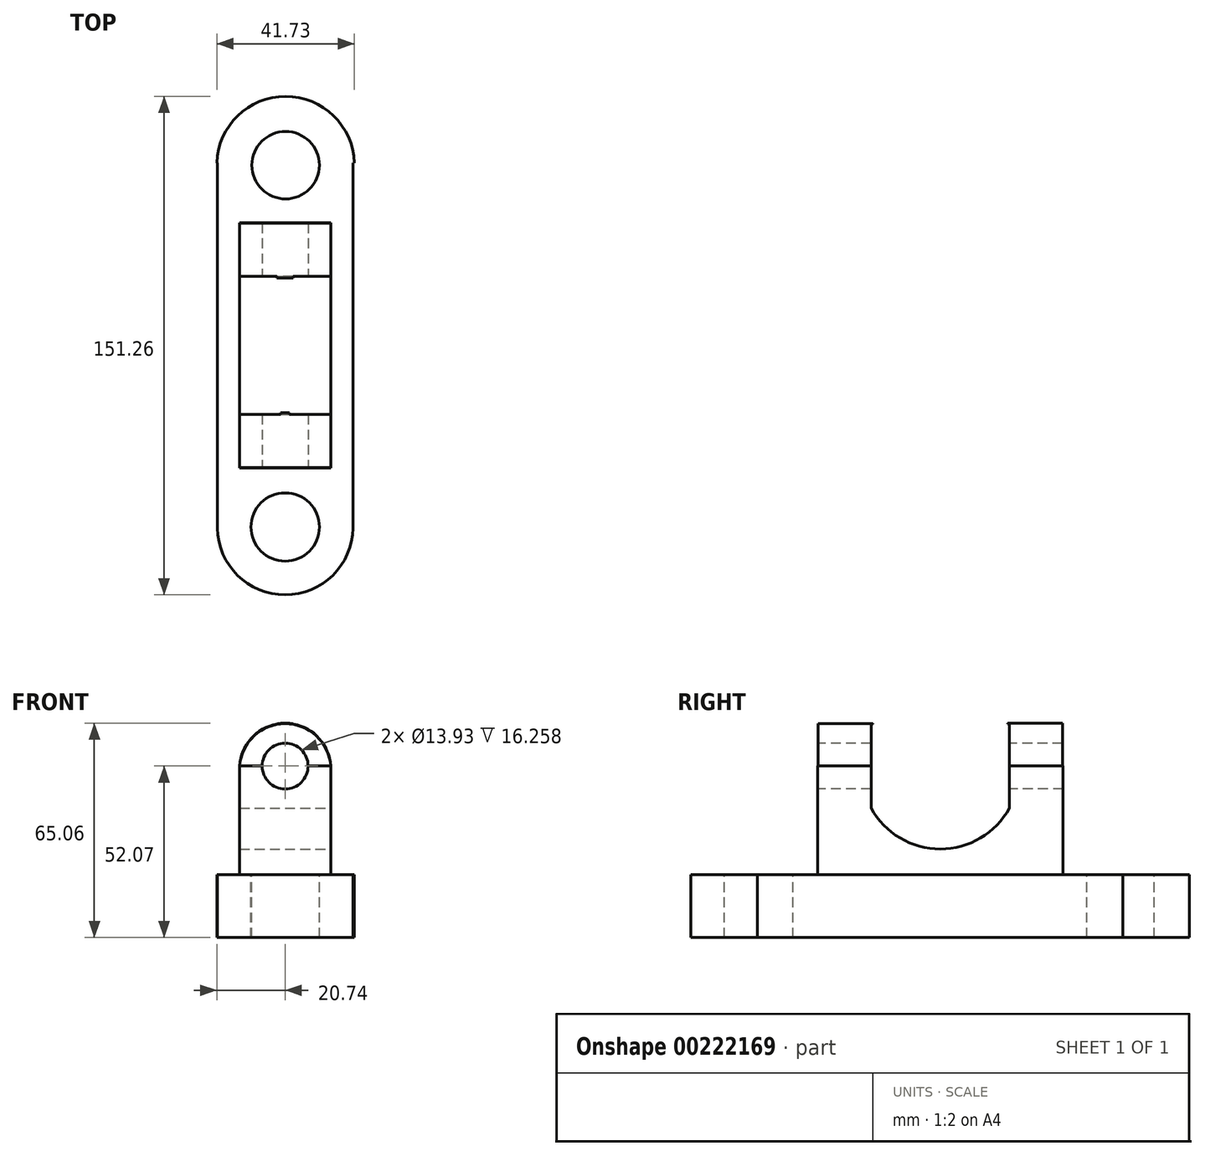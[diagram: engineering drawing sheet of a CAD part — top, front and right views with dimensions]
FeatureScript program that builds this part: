
annotation { "Feature Type Name" : "Feature", "Feature Type Description" : "" }
export const myFeature = defineFeature(function(context is Context, id is Id, definition is map)
    precondition{}
    {
        {
            var Q0;
            Q0=qCreatedBy(makeId("Top.planeOp"),FACE);
            var sketch = newSketch(context, id + "F0", { "sketchPlane" : qUnion([Q0])});
            skLineSegment(sketch, "E0.bottom", {"start": v(20.56, -55.45) * mm, "end": v(-20.56, -55.45) * mm});
            skLineSegment(sketch, "E0.top", {"start": v(20.56, 55.45) * mm, "end": v(-20.56, 55.45) * mm});
            skLineSegment(sketch, "E0.left", {"start": v(20.56, -55.45) * mm, "end": v(20.56, 55.45) * mm});
            skLineSegment(sketch, "E0.right", {"start": v(-20.56, -55.45) * mm, "end": v(-20.56, 55.45) * mm});
            skPoint(sketch, "E0.middle", {"position": v(0, 0) * mm});
            skSolve(sketch);
        }
        {
            var Q0;
            Q0 = qSketchRegion(id + "F0", true);
            extrude(context, id + "F1", {"entities" : qUnion([Q0]), "depth" : 19.05 * mm});
        }
        {
            var Q0;
            Q0=qCreatedBy(makeId("Top.planeOp"),FACE);
            var sketch = newSketch(context, id + "F2", { "sketchPlane" : qUnion([Q0])});
            skArc(sketch, "E1", {"start": v(21, 55.43) * mm, "mid": v(0.13, 75.58) * mm, "end": v(-20.74, 55.43) * mm});
            skLineSegment(sketch, "E2", {"start": v(-20.74, 55.43) * mm, "end": v(21, 55.43) * mm});
            skSolve(sketch);
        }
        {
            var Q0;
            Q0=makeQuery(id+"F2.imprint","IMPRINT",FACE,{"disambiguationData":[TD([[makeQuery(id+"F2.imprint","IMPRINT",EDGE,{"derivedFrom":sQuery(id+"F2.wireOp",EDGE,"E1")}),1.0]])]});
            extrude(context, id + "F3", {"entities" : qUnion([Q0]), "operationType" : NewBodyOperationType.ADD, "depth" : 19.05 * mm});
        }
        {
            var Q0;
            Q0=qCreatedBy(makeId("Top.planeOp"),FACE);
            var sketch = newSketch(context, id + "F4", { "sketchPlane" : qUnion([Q0])});
            skLineSegment(sketch, "E3.0", {"start": v(20.56, -55.45) * mm, "end": v(-20.56, -55.45) * mm});
            skArc(sketch, "E4", {"start": v(-20.56, -55.45) * mm, "mid": v(0, -75.68) * mm, "end": v(20.56, -55.45) * mm});
            skSolve(sketch);
        }
        {
            var Q0;
            Q0 = qSketchRegion(id + "F4", true);
            extrude(context, id + "F5", {"entities" : qUnion([Q0]), "operationType" : NewBodyOperationType.ADD, "depth" : 19.05 * mm});
        }
        {
            var Q0;
            Q0=makeQuery(id+"F5.boolean.opBoolean","MERGE",FACE,{"derivedFrom":[makeQuery(id+"F3.boolean.opBoolean","MERGE",FACE,{"derivedFrom":[makeQuery(id+"F1.opExtrude","CAP_FACE",FACE,{"disambiguationData":[OSD([sQuery(id+"F0.wireOp",EDGE,"E0.bottom"),sQuery(id+"F0.wireOp",EDGE,"E0.top"),sQuery(id+"F0.wireOp",EDGE,"E0.left"),sQuery(id+"F0.wireOp",EDGE,"E0.right")])],"isStart":false}),makeQuery(id+"F3.opExtrude","CAP_FACE",FACE,{"disambiguationData":[OSD([sQuery(id+"F2.wireOp",EDGE,"E1"),sQuery(id+"F2.wireOp",EDGE,"E2")])],"isStart":false})]}),makeQuery(id+"F5.opExtrude","CAP_FACE",FACE,{"disambiguationData":[OSD([sQuery(id+"F4.wireOp",EDGE,"E3.0"),sQuery(id+"F4.wireOp",EDGE,"E4")])],"isStart":false})]});
            var sketch = newSketch(context, id + "F6", { "sketchPlane" : qUnion([Q0])});
            skLineSegment(sketch, "E5.bottom", {"start": v(13.83, -37.25) * mm, "end": v(-13.83, -37.25) * mm});
            skLineSegment(sketch, "E5.top", {"start": v(13.83, 37.25) * mm, "end": v(-13.83, 37.25) * mm});
            skLineSegment(sketch, "E5.left", {"start": v(13.83, -37.25) * mm, "end": v(13.83, 37.25) * mm});
            skLineSegment(sketch, "E5.right", {"start": v(-13.83, -37.25) * mm, "end": v(-13.83, 37.25) * mm});
            skPoint(sketch, "E5.middle", {"position": v(0, 0) * mm});
            skSolve(sketch);
        }
        {
            var Q0;
            Q0 = qSketchRegion(id + "F6", true);
            extrude(context, id + "F7", {"entities" : qUnion([Q0]), "operationType" : NewBodyOperationType.ADD, "depth" : 33.02 * mm});
        }
        {
            var Q0;
            Q0=qCreatedBy(makeId("Front.planeOp"),FACE);
            var sketch = newSketch(context, id + "F8", { "sketchPlane" : qUnion([Q0])});
            skLineSegment(sketch, "E6.0", {"start": v(13.83, 52.07) * mm, "end": v(-13.83, 52.07) * mm});
            skArc(sketch, "E7", {"start": v(13.83, 52.07) * mm, "mid": v(0, 64.9) * mm, "end": v(-13.83, 52.07) * mm});
            skSolve(sketch);
        }
        {
            var Q0;
            Q0 = qSketchRegion(id + "F8", true);
            extrude(context, id + "F9", {"entities" : qUnion([Q0]), "operationType" : NewBodyOperationType.ADD, "depth" : 37.08 * mm});
        }
        {
            var Q0;
            Q0=qCreatedBy(makeId("Front.planeOp"),FACE);
            var sketch = newSketch(context, id + "F10", { "sketchPlane" : qUnion([Q0])});
            skLineSegment(sketch, "E8.0", {"start": v(13.83, 52.07) * mm, "end": v(-13.83, 52.07) * mm});
            skArc(sketch, "E9", {"start": v(13.83, 52.07) * mm, "mid": v(0, 65.06) * mm, "end": v(-13.83, 52.07) * mm});
            skSolve(sketch);
        }
        {
            var Q0;
            Q0 = qSketchRegion(id + "F10", true);
            extrude(context, id + "F11", {"entities" : qUnion([Q0]), "operationType" : NewBodyOperationType.ADD, "oppositeDirection" : true, "depth" : 37.08 * mm});
        }
        {
            var Q0;
            Q0=makeQuery(id+"F7.opExtrude","SWEPT_FACE",FACE,{"disambiguationData":[OSD([sQuery(id+"F6.wireOp",EDGE,"E5.bottom")])]});
            var sketch = newSketch(context, id + "F12", { "sketchPlane" : qUnion([Q0])});
            skCircle(sketch, "E10", {"center": v(0, 52.07) * mm, "radius": 6.96 * mm});
            skSolve(sketch);
        }
        {
            var Q0;
            Q0 = qSketchRegion(id + "F12", true);
            extrude(context, id + "F13", {"entities" : qUnion([Q0]), "operationType" : NewBodyOperationType.REMOVE, "endBound" : BoundingType.THROUGH_ALL, "oppositeDirection" : true, "depth" : 25.4 * mm});
        }
        {
            var Q0;
            Q0=makeQuery(id+"F7.opExtrude","SWEPT_FACE",FACE,{"disambiguationData":[OSD([sQuery(id+"F6.wireOp",EDGE,"E5.left")])]});
            var sketch = newSketch(context, id + "F14", { "sketchPlane" : qUnion([Q0])});
            skLineSegment(sketch, "E11.bottom", {"start": v(-21, 39.3) * mm, "end": v(21, 39.3) * mm});
            skLineSegment(sketch, "E11.top", {"start": v(-21, 64.84) * mm, "end": v(21, 64.84) * mm});
            skLineSegment(sketch, "E11.left", {"start": v(-21, 39.3) * mm, "end": v(-21, 64.84) * mm});
            skLineSegment(sketch, "E11.right", {"start": v(21, 39.3) * mm, "end": v(21, 64.84) * mm});
            skPoint(sketch, "E11.middle", {"position": v(0, 52.07) * mm});
            skArc(sketch, "E12", {"start": v(-21, 39.3) * mm, "mid": v(0, 26.9) * mm, "end": v(21, 39.3) * mm});
            skSolve(sketch);
        }
        {
            var Q0;
            Q0 = qSketchRegion(id + "F14", true);
            extrude(context, id + "F15", {"entities" : qUnion([Q0]), "operationType" : NewBodyOperationType.REMOVE, "endBound" : BoundingType.THROUGH_ALL, "oppositeDirection" : true, "depth" : 25.4 * mm});
        }
        {
            var Q0;
            Q0=makeQuery(id+"F7.opExtrude","SWEPT_FACE",FACE,{"disambiguationData":[OSD([sQuery(id+"F6.wireOp",EDGE,"E5.right")])]});
            var sketch = newSketch(context, id + "F16", { "sketchPlane" : qUnion([Q0])});
            skLineSegment(sketch, "E13.bottom", {"start": v(-20.48, 66.95) * mm, "end": v(20.48, 66.95) * mm});
            skLineSegment(sketch, "E13.top", {"start": v(-20.48, 46.47) * mm, "end": v(20.48, 46.47) * mm});
            skLineSegment(sketch, "E13.left", {"start": v(-20.48, 66.95) * mm, "end": v(-20.48, 46.47) * mm});
            skLineSegment(sketch, "E13.right", {"start": v(20.48, 66.95) * mm, "end": v(20.48, 46.47) * mm});
            skPoint(sketch, "E13.middle", {"position": v(0, 56.71) * mm});
            skSolve(sketch);
        }
        {
            var Q0;
            Q0 = qSketchRegion(id + "F16", true);
            extrude(context, id + "F17", {"entities" : qUnion([Q0]), "operationType" : NewBodyOperationType.REMOVE, "endBound" : BoundingType.THROUGH_ALL, "oppositeDirection" : true, "depth" : 25.4 * mm});
        }
        {
            var Q0;
            Q0=makeQuery(id+"F5.boolean.opBoolean","MERGE",FACE,{"derivedFrom":[makeQuery(id+"F3.boolean.opBoolean","MERGE",FACE,{"derivedFrom":[makeQuery(id+"F1.opExtrude","CAP_FACE",FACE,{"disambiguationData":[OSD([sQuery(id+"F0.wireOp",EDGE,"E0.bottom"),sQuery(id+"F0.wireOp",EDGE,"E0.top"),sQuery(id+"F0.wireOp",EDGE,"E0.left"),sQuery(id+"F0.wireOp",EDGE,"E0.right")])],"isStart":false}),makeQuery(id+"F3.opExtrude","CAP_FACE",FACE,{"disambiguationData":[OSD([sQuery(id+"F2.wireOp",EDGE,"E1"),sQuery(id+"F2.wireOp",EDGE,"E2")])],"isStart":false})]}),makeQuery(id+"F5.opExtrude","CAP_FACE",FACE,{"disambiguationData":[OSD([sQuery(id+"F4.wireOp",EDGE,"E3.0"),sQuery(id+"F4.wireOp",EDGE,"E4")])],"isStart":false})]});
            var sketch = newSketch(context, id + "F18", { "sketchPlane" : qUnion([Q0])});
            skCircle(sketch, "E14", {"center": v(0.13, 54.7) * mm, "radius": 10.24 * mm});
            skSolve(sketch);
        }
        {
            var Q0;
            Q0 = qSketchRegion(id + "F18", true);
            extrude(context, id + "F19", {"entities" : qUnion([Q0]), "operationType" : NewBodyOperationType.REMOVE, "endBound" : BoundingType.THROUGH_ALL, "oppositeDirection" : true, "depth" : 25.4 * mm});
        }
        {
            var Q0;
            Q0=makeQuery(id+"F5.boolean.opBoolean","MERGE",FACE,{"derivedFrom":[makeQuery(id+"F3.boolean.opBoolean","MERGE",FACE,{"derivedFrom":[makeQuery(id+"F1.opExtrude","CAP_FACE",FACE,{"disambiguationData":[OSD([sQuery(id+"F0.wireOp",EDGE,"E0.bottom"),sQuery(id+"F0.wireOp",EDGE,"E0.top"),sQuery(id+"F0.wireOp",EDGE,"E0.left"),sQuery(id+"F0.wireOp",EDGE,"E0.right")])],"isStart":false}),makeQuery(id+"F3.opExtrude","CAP_FACE",FACE,{"disambiguationData":[OSD([sQuery(id+"F2.wireOp",EDGE,"E1"),sQuery(id+"F2.wireOp",EDGE,"E2")])],"isStart":false})]}),makeQuery(id+"F5.opExtrude","CAP_FACE",FACE,{"disambiguationData":[OSD([sQuery(id+"F4.wireOp",EDGE,"E3.0"),sQuery(id+"F4.wireOp",EDGE,"E4")])],"isStart":false})]});
            var sketch = newSketch(context, id + "F20", { "sketchPlane" : qUnion([Q0])});
            skCircle(sketch, "E15", {"center": v(0, -55.12) * mm, "radius": 10.36 * mm});
            skSolve(sketch);
        }
        {
            var Q0;
            Q0 = qSketchRegion(id + "F20", true);
            extrude(context, id + "F21", {"entities" : qUnion([Q0]), "operationType" : NewBodyOperationType.REMOVE, "endBound" : BoundingType.THROUGH_ALL, "oppositeDirection" : true, "depth" : 25.4 * mm});
        }
    });
